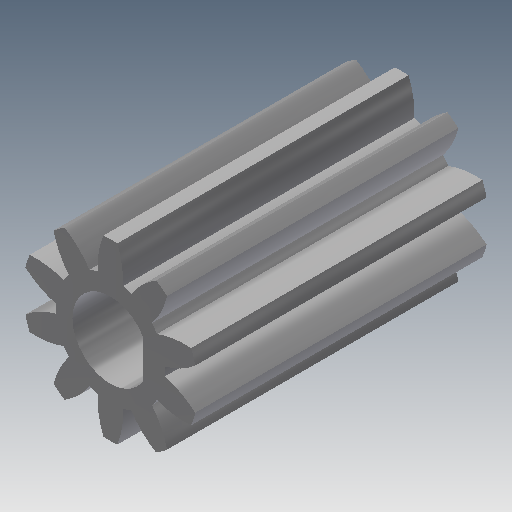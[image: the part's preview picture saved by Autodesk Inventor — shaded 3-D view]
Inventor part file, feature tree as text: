
AUTODESK INVENTOR PART (.ipt)
format: ipt  version: 2019.4 (Build 234330000, 330)  size: 222,208 bytes
history: native  units: mm (DEFAULTED — no unit token found)
features: other x6, plane x3, sketch x3, extrude x2, reference x1
ambient origin geometry x8: Origin, YZ Plane, XZ Plane, XY Plane, X Axis, Y Axis, Z Axis, Center Point
bodies: Solid1 (feature_tree)
feature tree (15):
  extrude  "Extrusion1"  Depth=20.0mm TaperAngle=0.0deg
  plane  "Work Plane2"
  plane  "Work Plane8"
  plane  "Work Plane9"
  other  "Spur Gear"
  extrude  "Extrusion2"  Depth=10.0mm TaperAngle=0.0deg
  sketch  "Sketch1"  dims[d0=12.0mm d1=20.0mm d2=0.0mm]
  sketch  "Sketch2"  dims[d3=10.0mm d4=10.0mm d5=0.0mm]
  other  "Srf1"
  sketch  "Sketch3"  dims[d16=13.0mm d17=0.0mm d34=3.141593mm d39=0.0mm d41=0.0mm d43=13.0mm d46=13.0mm d47=0.0mm d48=0.0mm d49=0.1mm d50=10.0mm d51=0.0mm]
  reference  "Reference1"
  other  "Pitch Diameter"
  other  "Assembly_Opentrons_Autofocus_v2.iam"
  other  "00_NEMA11:2"
  other  "Welle_11_2"
